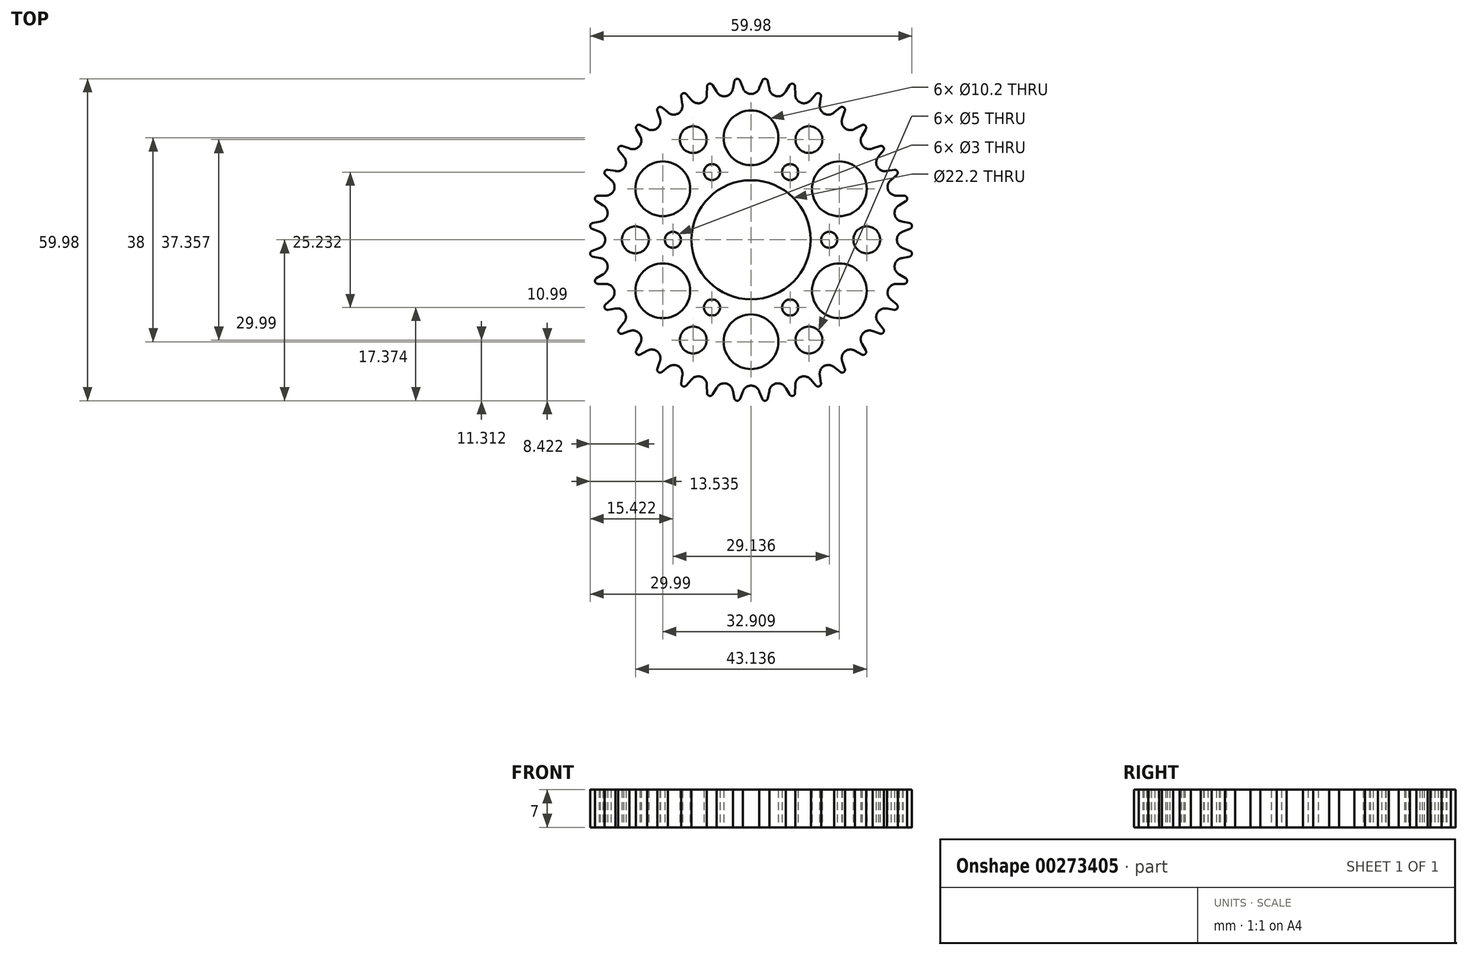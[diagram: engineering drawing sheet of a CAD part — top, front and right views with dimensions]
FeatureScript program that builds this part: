
annotation { "Feature Type Name" : "Feature", "Feature Type Description" : "" }
export const myFeature = defineFeature(function(context is Context, id is Id, definition is map)
    precondition{}
    {
        {
            var Q0;
            Q0=qCreatedBy(makeId("Top.planeOp"),FACE);
            var sketch = newSketch(context, id + "F0", { "sketchPlane" : qUnion([Q0])});
            skCircle(sketch, "E0", {"center": v(0, 0) * mm, "radius": 11.1 * mm});
            skCircle(sketch, "E1", {"center": v(0, 19) * mm, "radius": 5.1 * mm});
            skCircle(sketch, "E2.1.0", {"center": v(-16.45, 9.5) * mm, "radius": 5.1 * mm});
            skCircle(sketch, "E2.2.0", {"center": v(-16.45, -9.5) * mm, "radius": 5.1 * mm});
            skCircle(sketch, "E3.1.3.0", {"center": v(0, -19) * mm, "radius": 5.1 * mm});
            skCircle(sketch, "E3.1.4.0", {"center": v(16.45, -9.5) * mm, "radius": 5.1 * mm});
            skCircle(sketch, "E3.1.5.0", {"center": v(16.45, 9.5) * mm, "radius": 5.1 * mm});
            skCircle(sketch, "E4", {"center": v(0, 0) * mm, "radius": 19 * mm, "construction": true});
            skLineSegment(sketch, "E5", {"start": v(0, 0) * mm, "end": v(19, 0) * mm, "construction": true});
            skLineSegment(sketch, "E6", {"start": v(0, 0) * mm, "end": v(14.06, 24.35) * mm, "construction": true});
            skCircle(sketch, "E7", {"center": v(10.78, 18.68) * mm, "radius": 2.5 * mm});
            skCircle(sketch, "E8", {"center": v(7.28, 12.62) * mm, "radius": 1.5 * mm});
            skCircle(sketch, "E9.1.0", {"center": v(-7.28, 12.62) * mm, "radius": 1.5 * mm});
            skCircle(sketch, "E9.1.1", {"center": v(-10.78, 18.68) * mm, "radius": 2.5 * mm});
            skCircle(sketch, "E9.2.0", {"center": v(-14.57, 0) * mm, "radius": 1.5 * mm});
            skCircle(sketch, "E9.2.1", {"center": v(-21.57, 0) * mm, "radius": 2.5 * mm});
            skCircle(sketch, "E9.3.0", {"center": v(-7.28, -12.62) * mm, "radius": 1.5 * mm});
            skCircle(sketch, "E9.3.1", {"center": v(-10.78, -18.68) * mm, "radius": 2.5 * mm});
            skCircle(sketch, "E9.4.0", {"center": v(7.28, -12.62) * mm, "radius": 1.5 * mm});
            skCircle(sketch, "E9.4.1", {"center": v(10.78, -18.68) * mm, "radius": 2.5 * mm});
            skCircle(sketch, "E9.5.0", {"center": v(14.57, 0) * mm, "radius": 1.5 * mm});
            skCircle(sketch, "E9.5.1", {"center": v(21.57, 0) * mm, "radius": 2.5 * mm});
            skArc(sketch, "E10", {"start": v(-1.54, 28.32) * mm, "mid": v(0, 27.18) * mm, "end": v(1.54, 28.32) * mm});
            skLineSegment(sketch, "E11", {"start": v(1.54, 28.32) * mm, "end": v(2.06, 29.64) * mm});
            skLineSegment(sketch, "E12.MirrorCS", {"start": v(-1.54, 28.32) * mm, "end": v(-2.06, 29.64) * mm});
            skLineSegment(sketch, "E13.1.0", {"start": v(-6.44, 27.62) * mm, "end": v(-7.17, 28.83) * mm});
            skArc(sketch, "E13.1.1", {"start": v(-6.44, 27.62) * mm, "mid": v(-4.72, 26.77) * mm, "end": v(-3.4, 28.16) * mm});
            skLineSegment(sketch, "E13.1.2", {"start": v(-3.4, 28.16) * mm, "end": v(-3.12, 29.54) * mm});
            skLineSegment(sketch, "E13.2.0", {"start": v(-11.14, 26.09) * mm, "end": v(-12.07, 27.15) * mm});
            skArc(sketch, "E13.2.1", {"start": v(-11.14, 26.09) * mm, "mid": v(-9.3, 25.54) * mm, "end": v(-8.24, 27.14) * mm});
            skLineSegment(sketch, "E13.2.2", {"start": v(-8.24, 27.14) * mm, "end": v(-8.2, 28.55) * mm});
            skLineSegment(sketch, "E13.3.0", {"start": v(-15.5, 23.76) * mm, "end": v(-16.6, 24.64) * mm});
            skArc(sketch, "E13.3.1", {"start": v(-15.5, 23.76) * mm, "mid": v(-13.59, 23.54) * mm, "end": v(-12.82, 25.3) * mm});
            skLineSegment(sketch, "E13.3.2", {"start": v(-12.82, 25.3) * mm, "end": v(-13.04, 26.7) * mm});
            skLineSegment(sketch, "E13.4.0", {"start": v(-19.39, 20.7) * mm, "end": v(-20.62, 21.38) * mm});
            skArc(sketch, "E13.4.1", {"start": v(-19.39, 20.7) * mm, "mid": v(-17.47, 20.82) * mm, "end": v(-17.02, 22.69) * mm});
            skLineSegment(sketch, "E13.4.2", {"start": v(-17.02, 22.69) * mm, "end": v(-17.48, 24.02) * mm});
            skLineSegment(sketch, "E13.5.0", {"start": v(-22.69, 17.02) * mm, "end": v(-24.02, 17.48) * mm});
            skArc(sketch, "E13.5.1", {"start": v(-22.69, 17.02) * mm, "mid": v(-20.82, 17.47) * mm, "end": v(-20.7, 19.39) * mm});
            skLineSegment(sketch, "E13.5.2", {"start": v(-20.7, 19.39) * mm, "end": v(-21.38, 20.62) * mm});
            skLineSegment(sketch, "E13.6.0", {"start": v(-25.3, 12.82) * mm, "end": v(-26.7, 13.04) * mm});
            skArc(sketch, "E13.6.1", {"start": v(-25.3, 12.82) * mm, "mid": v(-23.54, 13.59) * mm, "end": v(-23.76, 15.5) * mm});
            skLineSegment(sketch, "E13.6.2", {"start": v(-23.76, 15.5) * mm, "end": v(-24.64, 16.6) * mm});
            skLineSegment(sketch, "E13.7.0", {"start": v(-27.14, 8.24) * mm, "end": v(-28.55, 8.2) * mm});
            skArc(sketch, "E13.7.1", {"start": v(-27.14, 8.24) * mm, "mid": v(-25.54, 9.3) * mm, "end": v(-26.09, 11.14) * mm});
            skLineSegment(sketch, "E13.7.2", {"start": v(-26.09, 11.14) * mm, "end": v(-27.15, 12.07) * mm});
            skLineSegment(sketch, "E13.8.0", {"start": v(-28.16, 3.4) * mm, "end": v(-29.54, 3.12) * mm});
            skArc(sketch, "E13.8.1", {"start": v(-28.16, 3.4) * mm, "mid": v(-26.77, 4.72) * mm, "end": v(-27.62, 6.44) * mm});
            skLineSegment(sketch, "E13.8.2", {"start": v(-27.62, 6.44) * mm, "end": v(-28.83, 7.17) * mm});
            skLineSegment(sketch, "E13.9.0", {"start": v(-28.32, -1.54) * mm, "end": v(-29.64, -2.06) * mm});
            skArc(sketch, "E13.9.1", {"start": v(-28.32, -1.54) * mm, "mid": v(-27.18, 0) * mm, "end": v(-28.32, 1.54) * mm});
            skLineSegment(sketch, "E13.9.2", {"start": v(-28.32, 1.54) * mm, "end": v(-29.64, 2.06) * mm});
            skLineSegment(sketch, "E13.10.0", {"start": v(-27.62, -6.44) * mm, "end": v(-28.83, -7.17) * mm});
            skArc(sketch, "E13.10.1", {"start": v(-27.62, -6.44) * mm, "mid": v(-26.77, -4.72) * mm, "end": v(-28.16, -3.4) * mm});
            skLineSegment(sketch, "E13.10.2", {"start": v(-28.16, -3.4) * mm, "end": v(-29.54, -3.12) * mm});
            skLineSegment(sketch, "E13.11.0", {"start": v(-26.09, -11.14) * mm, "end": v(-27.15, -12.07) * mm});
            skArc(sketch, "E13.11.1", {"start": v(-26.09, -11.14) * mm, "mid": v(-25.54, -9.3) * mm, "end": v(-27.14, -8.24) * mm});
            skLineSegment(sketch, "E13.11.2", {"start": v(-27.14, -8.24) * mm, "end": v(-28.55, -8.2) * mm});
            skLineSegment(sketch, "E13.12.0", {"start": v(-23.76, -15.5) * mm, "end": v(-24.64, -16.6) * mm});
            skArc(sketch, "E13.12.1", {"start": v(-23.76, -15.5) * mm, "mid": v(-23.54, -13.59) * mm, "end": v(-25.3, -12.82) * mm});
            skLineSegment(sketch, "E13.12.2", {"start": v(-25.3, -12.82) * mm, "end": v(-26.7, -13.04) * mm});
            skLineSegment(sketch, "E13.13.0", {"start": v(-20.7, -19.39) * mm, "end": v(-21.38, -20.62) * mm});
            skArc(sketch, "E13.13.1", {"start": v(-20.7, -19.39) * mm, "mid": v(-20.82, -17.47) * mm, "end": v(-22.69, -17.02) * mm});
            skLineSegment(sketch, "E13.13.2", {"start": v(-22.69, -17.02) * mm, "end": v(-24.02, -17.48) * mm});
            skLineSegment(sketch, "E13.14.0", {"start": v(-17.02, -22.69) * mm, "end": v(-17.48, -24.02) * mm});
            skArc(sketch, "E13.14.1", {"start": v(-17.02, -22.69) * mm, "mid": v(-17.47, -20.82) * mm, "end": v(-19.39, -20.7) * mm});
            skLineSegment(sketch, "E13.14.2", {"start": v(-19.39, -20.7) * mm, "end": v(-20.62, -21.38) * mm});
            skLineSegment(sketch, "E13.15.0", {"start": v(-12.82, -25.3) * mm, "end": v(-13.04, -26.7) * mm});
            skArc(sketch, "E13.15.1", {"start": v(-12.82, -25.3) * mm, "mid": v(-13.59, -23.54) * mm, "end": v(-15.5, -23.76) * mm});
            skLineSegment(sketch, "E13.15.2", {"start": v(-15.5, -23.76) * mm, "end": v(-16.6, -24.64) * mm});
            skLineSegment(sketch, "E13.16.0", {"start": v(-8.24, -27.14) * mm, "end": v(-8.2, -28.55) * mm});
            skArc(sketch, "E13.16.1", {"start": v(-8.24, -27.14) * mm, "mid": v(-9.3, -25.54) * mm, "end": v(-11.14, -26.09) * mm});
            skLineSegment(sketch, "E13.16.2", {"start": v(-11.14, -26.09) * mm, "end": v(-12.07, -27.15) * mm});
            skLineSegment(sketch, "E13.17.0", {"start": v(-3.4, -28.16) * mm, "end": v(-3.12, -29.54) * mm});
            skArc(sketch, "E13.17.1", {"start": v(-3.4, -28.16) * mm, "mid": v(-4.72, -26.77) * mm, "end": v(-6.44, -27.62) * mm});
            skLineSegment(sketch, "E13.17.2", {"start": v(-6.44, -27.62) * mm, "end": v(-7.17, -28.83) * mm});
            skLineSegment(sketch, "E13.18.0", {"start": v(1.54, -28.32) * mm, "end": v(2.06, -29.64) * mm});
            skArc(sketch, "E13.18.1", {"start": v(1.54, -28.32) * mm, "mid": v(0, -27.18) * mm, "end": v(-1.54, -28.32) * mm});
            skLineSegment(sketch, "E13.18.2", {"start": v(-1.54, -28.32) * mm, "end": v(-2.06, -29.64) * mm});
            skLineSegment(sketch, "E13.19.0", {"start": v(6.44, -27.62) * mm, "end": v(7.17, -28.83) * mm});
            skArc(sketch, "E13.19.1", {"start": v(6.44, -27.62) * mm, "mid": v(4.72, -26.77) * mm, "end": v(3.4, -28.16) * mm});
            skLineSegment(sketch, "E13.19.2", {"start": v(3.4, -28.16) * mm, "end": v(3.12, -29.54) * mm});
            skLineSegment(sketch, "E13.20.0", {"start": v(11.14, -26.09) * mm, "end": v(12.07, -27.15) * mm});
            skArc(sketch, "E13.20.1", {"start": v(11.14, -26.09) * mm, "mid": v(9.3, -25.54) * mm, "end": v(8.24, -27.14) * mm});
            skLineSegment(sketch, "E13.20.2", {"start": v(8.24, -27.14) * mm, "end": v(8.2, -28.55) * mm});
            skLineSegment(sketch, "E13.21.0", {"start": v(15.5, -23.76) * mm, "end": v(16.6, -24.64) * mm});
            skArc(sketch, "E13.21.1", {"start": v(15.5, -23.76) * mm, "mid": v(13.59, -23.54) * mm, "end": v(12.82, -25.3) * mm});
            skLineSegment(sketch, "E13.21.2", {"start": v(12.82, -25.3) * mm, "end": v(13.04, -26.7) * mm});
            skLineSegment(sketch, "E13.22.0", {"start": v(19.39, -20.7) * mm, "end": v(20.62, -21.38) * mm});
            skArc(sketch, "E13.22.1", {"start": v(19.39, -20.7) * mm, "mid": v(17.47, -20.82) * mm, "end": v(17.02, -22.69) * mm});
            skLineSegment(sketch, "E13.22.2", {"start": v(17.02, -22.69) * mm, "end": v(17.48, -24.02) * mm});
            skLineSegment(sketch, "E13.23.0", {"start": v(22.69, -17.02) * mm, "end": v(24.02, -17.48) * mm});
            skArc(sketch, "E13.23.1", {"start": v(22.69, -17.02) * mm, "mid": v(20.82, -17.47) * mm, "end": v(20.7, -19.39) * mm});
            skLineSegment(sketch, "E13.23.2", {"start": v(20.7, -19.39) * mm, "end": v(21.38, -20.62) * mm});
            skLineSegment(sketch, "E13.24.0", {"start": v(25.3, -12.82) * mm, "end": v(26.7, -13.04) * mm});
            skArc(sketch, "E13.24.1", {"start": v(25.3, -12.82) * mm, "mid": v(23.54, -13.59) * mm, "end": v(23.76, -15.5) * mm});
            skLineSegment(sketch, "E13.24.2", {"start": v(23.76, -15.5) * mm, "end": v(24.64, -16.6) * mm});
            skLineSegment(sketch, "E13.25.0", {"start": v(27.14, -8.24) * mm, "end": v(28.55, -8.2) * mm});
            skArc(sketch, "E13.25.1", {"start": v(27.14, -8.24) * mm, "mid": v(25.54, -9.3) * mm, "end": v(26.09, -11.14) * mm});
            skLineSegment(sketch, "E13.25.2", {"start": v(26.09, -11.14) * mm, "end": v(27.15, -12.07) * mm});
            skLineSegment(sketch, "E13.26.0", {"start": v(28.16, -3.4) * mm, "end": v(29.54, -3.12) * mm});
            skArc(sketch, "E13.26.1", {"start": v(28.16, -3.4) * mm, "mid": v(26.77, -4.72) * mm, "end": v(27.62, -6.44) * mm});
            skLineSegment(sketch, "E13.26.2", {"start": v(27.62, -6.44) * mm, "end": v(28.83, -7.17) * mm});
            skLineSegment(sketch, "E13.27.0", {"start": v(28.32, 1.54) * mm, "end": v(29.64, 2.06) * mm});
            skArc(sketch, "E13.27.1", {"start": v(28.32, 1.54) * mm, "mid": v(27.18, 0) * mm, "end": v(28.32, -1.54) * mm});
            skLineSegment(sketch, "E13.27.2", {"start": v(28.32, -1.54) * mm, "end": v(29.64, -2.06) * mm});
            skLineSegment(sketch, "E13.28.0", {"start": v(27.62, 6.44) * mm, "end": v(28.83, 7.17) * mm});
            skArc(sketch, "E13.28.1", {"start": v(27.62, 6.44) * mm, "mid": v(26.77, 4.72) * mm, "end": v(28.16, 3.4) * mm});
            skLineSegment(sketch, "E13.28.2", {"start": v(28.16, 3.4) * mm, "end": v(29.54, 3.12) * mm});
            skLineSegment(sketch, "E13.29.0", {"start": v(26.09, 11.14) * mm, "end": v(27.15, 12.07) * mm});
            skArc(sketch, "E13.29.1", {"start": v(26.09, 11.14) * mm, "mid": v(25.54, 9.3) * mm, "end": v(27.14, 8.24) * mm});
            skLineSegment(sketch, "E13.29.2", {"start": v(27.14, 8.24) * mm, "end": v(28.55, 8.2) * mm});
            skLineSegment(sketch, "E14.1.30.0", {"start": v(23.76, 15.5) * mm, "end": v(24.64, 16.6) * mm});
            skArc(sketch, "E14.3.30.0", {"start": v(23.76, 15.5) * mm, "mid": v(23.54, 13.59) * mm, "end": v(25.3, 12.82) * mm});
            skLineSegment(sketch, "E14.7.30.0", {"start": v(25.3, 12.82) * mm, "end": v(26.7, 13.04) * mm});
            skLineSegment(sketch, "E15.1.31.0", {"start": v(20.7, 19.39) * mm, "end": v(21.38, 20.62) * mm});
            skArc(sketch, "E15.3.31.0", {"start": v(20.7, 19.39) * mm, "mid": v(20.82, 17.47) * mm, "end": v(22.69, 17.02) * mm});
            skLineSegment(sketch, "E15.7.31.0", {"start": v(22.69, 17.02) * mm, "end": v(24.02, 17.48) * mm});
            skLineSegment(sketch, "E16.1.32.0", {"start": v(17.02, 22.69) * mm, "end": v(17.48, 24.02) * mm});
            skArc(sketch, "E16.3.32.0", {"start": v(17.02, 22.69) * mm, "mid": v(17.47, 20.82) * mm, "end": v(19.39, 20.7) * mm});
            skLineSegment(sketch, "E16.7.32.0", {"start": v(19.39, 20.7) * mm, "end": v(20.62, 21.38) * mm});
            skLineSegment(sketch, "E16.1.33.0", {"start": v(12.82, 25.3) * mm, "end": v(13.04, 26.7) * mm});
            skArc(sketch, "E16.3.33.0", {"start": v(12.82, 25.3) * mm, "mid": v(13.59, 23.54) * mm, "end": v(15.5, 23.76) * mm});
            skLineSegment(sketch, "E16.7.33.0", {"start": v(15.5, 23.76) * mm, "end": v(16.6, 24.64) * mm});
            skLineSegment(sketch, "E17.1.34.0", {"start": v(8.24, 27.14) * mm, "end": v(8.2, 28.55) * mm});
            skArc(sketch, "E17.3.34.0", {"start": v(8.24, 27.14) * mm, "mid": v(9.3, 25.54) * mm, "end": v(11.14, 26.09) * mm});
            skLineSegment(sketch, "E17.7.34.0", {"start": v(11.14, 26.09) * mm, "end": v(12.07, 27.15) * mm});
            skLineSegment(sketch, "E17.1.35.0", {"start": v(3.4, 28.16) * mm, "end": v(3.12, 29.54) * mm});
            skArc(sketch, "E17.3.35.0", {"start": v(3.4, 28.16) * mm, "mid": v(4.72, 26.77) * mm, "end": v(6.44, 27.62) * mm});
            skLineSegment(sketch, "E17.7.35.0", {"start": v(6.44, 27.62) * mm, "end": v(7.17, 28.83) * mm});
            skArc(sketch, "E18", {"start": v(-2.06, 29.64) * mm, "mid": v(-2.62, 29.99) * mm, "end": v(-3.12, 29.54) * mm});
            skArc(sketch, "E19.1.0", {"start": v(-7.17, 28.83) * mm, "mid": v(-7.8, 29.08) * mm, "end": v(-8.2, 28.55) * mm});
            skArc(sketch, "E19.2.0", {"start": v(-12.07, 27.15) * mm, "mid": v(-12.72, 27.28) * mm, "end": v(-13.04, 26.7) * mm});
            skArc(sketch, "E19.3.0", {"start": v(-16.6, 24.64) * mm, "mid": v(-17.27, 24.66) * mm, "end": v(-17.48, 24.02) * mm});
            skArc(sketch, "E19.4.0", {"start": v(-20.62, 21.38) * mm, "mid": v(-21.29, 21.29) * mm, "end": v(-21.38, 20.62) * mm});
            skArc(sketch, "E19.5.0", {"start": v(-24.02, 17.48) * mm, "mid": v(-24.66, 17.27) * mm, "end": v(-24.64, 16.6) * mm});
            skArc(sketch, "E19.6.0", {"start": v(-26.7, 13.04) * mm, "mid": v(-27.28, 12.72) * mm, "end": v(-27.15, 12.07) * mm});
            skArc(sketch, "E19.7.0", {"start": v(-28.55, 8.2) * mm, "mid": v(-29.08, 7.8) * mm, "end": v(-28.83, 7.17) * mm});
            skArc(sketch, "E19.8.0", {"start": v(-29.54, 3.12) * mm, "mid": v(-29.99, 2.62) * mm, "end": v(-29.64, 2.06) * mm});
            skArc(sketch, "E19.9.0", {"start": v(-29.64, -2.06) * mm, "mid": v(-29.99, -2.62) * mm, "end": v(-29.54, -3.12) * mm});
            skArc(sketch, "E19.10.0", {"start": v(-28.83, -7.17) * mm, "mid": v(-29.08, -7.8) * mm, "end": v(-28.55, -8.2) * mm});
            skArc(sketch, "E19.11.0", {"start": v(-27.15, -12.07) * mm, "mid": v(-27.28, -12.72) * mm, "end": v(-26.7, -13.04) * mm});
            skArc(sketch, "E19.12.0", {"start": v(-24.64, -16.6) * mm, "mid": v(-24.66, -17.27) * mm, "end": v(-24.02, -17.48) * mm});
            skArc(sketch, "E19.13.0", {"start": v(-21.38, -20.62) * mm, "mid": v(-21.29, -21.29) * mm, "end": v(-20.62, -21.38) * mm});
            skArc(sketch, "E19.14.0", {"start": v(-17.48, -24.02) * mm, "mid": v(-17.27, -24.66) * mm, "end": v(-16.6, -24.64) * mm});
            skArc(sketch, "E19.15.0", {"start": v(-13.04, -26.7) * mm, "mid": v(-12.72, -27.28) * mm, "end": v(-12.07, -27.15) * mm});
            skArc(sketch, "E19.16.0", {"start": v(-8.2, -28.55) * mm, "mid": v(-7.8, -29.08) * mm, "end": v(-7.17, -28.83) * mm});
            skArc(sketch, "E19.17.0", {"start": v(-3.12, -29.54) * mm, "mid": v(-2.62, -29.99) * mm, "end": v(-2.06, -29.64) * mm});
            skArc(sketch, "E19.18.0", {"start": v(2.06, -29.64) * mm, "mid": v(2.62, -29.99) * mm, "end": v(3.12, -29.54) * mm});
            skArc(sketch, "E19.19.0", {"start": v(7.17, -28.83) * mm, "mid": v(7.8, -29.08) * mm, "end": v(8.2, -28.55) * mm});
            skArc(sketch, "E19.20.0", {"start": v(12.07, -27.15) * mm, "mid": v(12.72, -27.28) * mm, "end": v(13.04, -26.7) * mm});
            skArc(sketch, "E19.21.0", {"start": v(16.6, -24.64) * mm, "mid": v(17.27, -24.66) * mm, "end": v(17.48, -24.02) * mm});
            skArc(sketch, "E19.22.0", {"start": v(20.62, -21.38) * mm, "mid": v(21.29, -21.29) * mm, "end": v(21.38, -20.62) * mm});
            skArc(sketch, "E19.23.0", {"start": v(24.02, -17.48) * mm, "mid": v(24.66, -17.27) * mm, "end": v(24.64, -16.6) * mm});
            skArc(sketch, "E19.24.0", {"start": v(26.7, -13.04) * mm, "mid": v(27.28, -12.72) * mm, "end": v(27.15, -12.07) * mm});
            skArc(sketch, "E19.25.0", {"start": v(28.55, -8.2) * mm, "mid": v(29.08, -7.8) * mm, "end": v(28.83, -7.17) * mm});
            skArc(sketch, "E19.26.0", {"start": v(29.54, -3.12) * mm, "mid": v(29.99, -2.62) * mm, "end": v(29.64, -2.06) * mm});
            skArc(sketch, "E19.27.0", {"start": v(29.64, 2.06) * mm, "mid": v(29.99, 2.62) * mm, "end": v(29.54, 3.12) * mm});
            skArc(sketch, "E19.28.0", {"start": v(28.83, 7.17) * mm, "mid": v(29.08, 7.8) * mm, "end": v(28.55, 8.2) * mm});
            skArc(sketch, "E19.29.0", {"start": v(27.15, 12.07) * mm, "mid": v(27.28, 12.72) * mm, "end": v(26.7, 13.04) * mm});
            skArc(sketch, "E19.30.0", {"start": v(24.64, 16.6) * mm, "mid": v(24.66, 17.27) * mm, "end": v(24.02, 17.48) * mm});
            skArc(sketch, "E19.31.0", {"start": v(21.38, 20.62) * mm, "mid": v(21.29, 21.29) * mm, "end": v(20.62, 21.38) * mm});
            skArc(sketch, "E19.32.0", {"start": v(17.48, 24.02) * mm, "mid": v(17.27, 24.66) * mm, "end": v(16.6, 24.64) * mm});
            skArc(sketch, "E19.33.0", {"start": v(13.04, 26.7) * mm, "mid": v(12.72, 27.28) * mm, "end": v(12.07, 27.15) * mm});
            skArc(sketch, "E19.34.0", {"start": v(8.2, 28.55) * mm, "mid": v(7.8, 29.08) * mm, "end": v(7.17, 28.83) * mm});
            skArc(sketch, "E19.35.0", {"start": v(3.12, 29.54) * mm, "mid": v(2.62, 29.99) * mm, "end": v(2.06, 29.64) * mm});
            skSolve(sketch);
        }
        {
            var Q0;
            Q0=makeQuery(id+"F0.imprint","IMPRINT",FACE,{"disambiguationData":[TD([[makeQuery(id+"F0.imprint","IMPRINT",EDGE,{"derivedFrom":sQuery(id+"F0.wireOp",EDGE,"E0")}),-1.0]])]});
            extrude(context, id + "F1", {"entities" : qUnion([Q0]), "depth" : 7 * mm});
        }
    });
